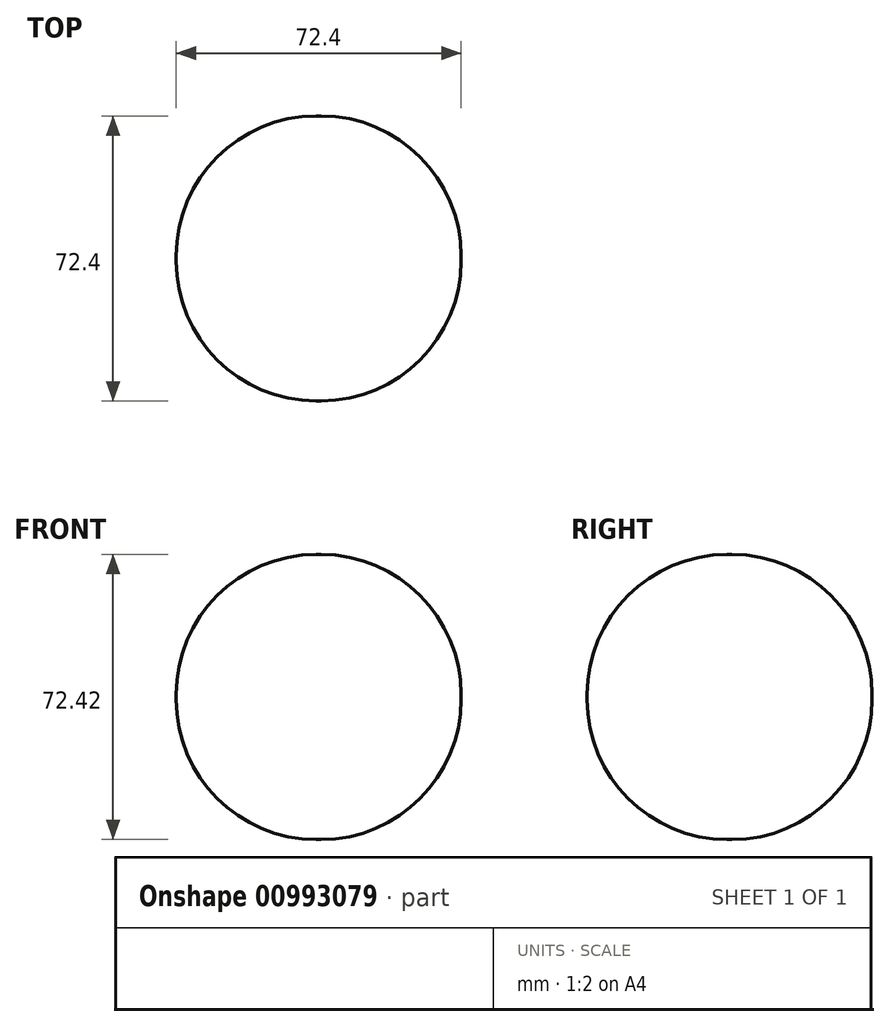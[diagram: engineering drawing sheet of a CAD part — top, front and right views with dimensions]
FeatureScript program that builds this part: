
annotation { "Feature Type Name" : "Feature", "Feature Type Description" : "" }
export const myFeature = defineFeature(function(context is Context, id is Id, definition is map)
    precondition{}
    {
        {
            var Q0;
            Q0=qCreatedBy(makeId("Top.planeOp"),FACE);
            var sketch = newSketch(context, id + "F0", { "sketchPlane" : qUnion([Q0])});
            skLineSegment(sketch, "E0.bottom", {"start": v(36.2, -36.2) * mm, "end": v(-36.2, -36.2) * mm});
            skLineSegment(sketch, "E0.top", {"start": v(36.2, 36.2) * mm, "end": v(-36.2, 36.2) * mm});
            skLineSegment(sketch, "E0.left", {"start": v(36.2, -36.2) * mm, "end": v(36.2, 36.2) * mm});
            skLineSegment(sketch, "E0.right", {"start": v(-36.2, -36.2) * mm, "end": v(-36.2, 36.2) * mm});
            skPoint(sketch, "E0.middle", {"position": v(0, 0) * mm});
            skSolve(sketch);
        }
        {
            var Q0;
            Q0 = qSketchRegion(id + "F0", true);
            extrude(context, id + "F1", {"entities" : qUnion([Q0]), "depth" : 72.42 * mm, "offsetDistance" : 25.4 * mm});
        }
        {
            var Q0;
            Q0=makeQuery(id+"F1.opExtrude","CAP_EDGE",EDGE,{"disambiguationData":[OSD([sQuery(id+"F0.wireOp",EDGE,"E0.right")])],"isStart":true});
            var Q1;
            Q1=makeQuery(id+"F1.opExtrude","CAP_EDGE",EDGE,{"disambiguationData":[OSD([sQuery(id+"F0.wireOp",EDGE,"E0.bottom")])],"isStart":true});
            var Q2;
            Q2=makeQuery(id+"F1.opExtrude","CAP_EDGE",EDGE,{"disambiguationData":[OSD([sQuery(id+"F0.wireOp",EDGE,"E0.left")])],"isStart":true});
            var Q3;
            Q3=makeQuery(id+"F1.opExtrude","SWEPT_EDGE",EDGE,{"disambiguationData":[OSD([sQuery(id+"F0.wireOp",EDGE,"E0.top"),sQuery(id+"F0.wireOp",EDGE,"E0.right")])]});
            var Q4;
            Q4=makeQuery(id+"F1.opExtrude","CAP_EDGE",EDGE,{"disambiguationData":[OSD([sQuery(id+"F0.wireOp",EDGE,"E0.top")])],"isStart":true});
            var Q5;
            Q5=makeQuery(id+"F1.opExtrude","SWEPT_EDGE",EDGE,{"disambiguationData":[OSD([sQuery(id+"F0.wireOp",EDGE,"E0.top"),sQuery(id+"F0.wireOp",EDGE,"E0.left")])]});
            var Q6;
            Q6=makeQuery(id+"F1.opExtrude","CAP_EDGE",EDGE,{"disambiguationData":[OSD([sQuery(id+"F0.wireOp",EDGE,"E0.top")])],"isStart":false});
            var Q7;
            Q7=makeQuery(id+"F1.opExtrude","SWEPT_EDGE",EDGE,{"disambiguationData":[OSD([sQuery(id+"F0.wireOp",EDGE,"E0.bottom"),sQuery(id+"F0.wireOp",EDGE,"E0.right")])]});
            var Q8;
            Q8=makeQuery(id+"F1.opExtrude","CAP_EDGE",EDGE,{"disambiguationData":[OSD([sQuery(id+"F0.wireOp",EDGE,"E0.right")])],"isStart":false});
            var Q9;
            Q9=makeQuery(id+"F1.opExtrude","CAP_EDGE",EDGE,{"disambiguationData":[OSD([sQuery(id+"F0.wireOp",EDGE,"E0.left")])],"isStart":false});
            var Q10;
            Q10=makeQuery(id+"F1.opExtrude","CAP_EDGE",EDGE,{"disambiguationData":[OSD([sQuery(id+"F0.wireOp",EDGE,"E0.bottom")])],"isStart":false});
            var Q11;
            Q11=makeQuery(id+"F1.opExtrude","SWEPT_EDGE",EDGE,{"disambiguationData":[OSD([sQuery(id+"F0.wireOp",EDGE,"E0.bottom"),sQuery(id+"F0.wireOp",EDGE,"E0.left")])]});
            fillet(context, id + "F2", {"entities" : qUnion([Q0, Q1, Q2, Q3, Q4, Q5, Q6, Q7, Q8, Q9, Q10, Q11]), "radius" : 35.57 * mm, "tangentPropagation" : true, "allowEdgeOverflow" : false});
        }
    });
